# Revit family: Plumbing_Joints_Aignep_Male-Tube-Ball-Valve-90720
name_source: partatom
category: Pipe Accessories
revit_build: Autodesk Revit 2018 (Build: 20170223_1515(x64)
units: mm (PartAtom-declared; Revit-internal decimal feet)

## family parameters
Always vertical = Yes
Cut with Voids When Loaded = No
OmniClass Number = 23.27.43.00
OmniClass Title = Pipe Fittings
Part Type = Valve - Breaks Into
Round Connector Dimension = Use Diameter
Shared = No
Work Plane-Based = No

## types (2) — shared parameters
Assembly Code = D2040100
BIMobject category = Valves
Description = Male-tube ball valve
Design country = Italy
Edition number = 1
IFC Classification = Pipe Fitting
Keynote = 15410
Lookup Table Name = Valve - Male-Tube-Ball-Valve-90720
M = 45 mm
Manufacturer = Aignep Spa
Manufacturer country = Italy
Manufacturer name = Aignep Spa
Material main = Brass
Model = 90720
OmniClass Code = 23-27 43 00
OmniClass Description = Pipe Fittings
Product Guid = 4f6d1d28-9b66-4a88-98e0-9f4e2d31ef23
Product Material = AIGNEP - Brass - Yellow
Product SKU = Male-Tube-Ball-Valve-90720
Product certification = https://www.aignep.com
Product data url = https://www.bimobject.com
Product family = INFINITY
Product group = Valves
Product name = Male-Tube Ball Valve - 90720
Product url = https://www.aignep.com
QR code = https://www.bimobject.com
URL = https://www.aignep.com

## per-type parameters (varying)
| type | A | B | C | CH1 | CH2 | Diameter | E | G | H | H Nut 1 | H Nut 2 | H1 | H2 | H3 | L | M Diameter 1 | M Diameter 2 | Nominal Diameter 01 | Nominal Diameter 02 | Nut Radius 1 | Nut Radius 2 | R | Tick Size 01 | Tick Size 02 |
| D 25 | 16.5 mm | 37 mm | 30.8 mm | 41 mm | 35 mm | 26 mm | 42.5 mm | 106 mm  [stored 0.347769 ft] | 47.5 mm | 11.06 mm | 9.64 mm | 4.069 mm | 1.38 mm | 8.83 mm | 115.1 mm | 43.5 mm | 45 mm | 25.000 mm | 19.050 mm | 21.5 mm | 21.5 mm | 7 mm  [stored 0.0229659 ft] | 20 mm  [stored 0.0656168 ft] | 15.24 mm |
| D 20 | 14 mm  [stored 0.0459318 ft] | 31.5 mm  [stored 0.103346 ft] | 29.3 mm  [stored 0.0961286 ft] | 32 mm  [stored 0.104987 ft] | 30 mm | 20.9 mm | 34.5 mm  [stored 0.113189 ft] | 88 mm  [stored 0.288714 ft] | 42 mm  [stored 0.137795 ft] | 13.084 mm | 6.578 mm | 2.34 mm  [stored 0.00767716 ft] | 0.9 mm  [stored 0.00295276 ft] | 7.817 mm  [stored 0.0256463 ft] | 99.35 mm  [stored 0.325951 ft] | 35.57 mm | 37 mm | 20.000 mm | 12.700 mm | 17 mm  [stored 0.0557743 ft] | 17 mm  [stored 0.0557743 ft] | 5 mm  [stored 0.0164042 ft] | 16 mm  [stored 0.0524934 ft] | 10.16 mm  [stored 0.0333333 ft] |

note: [stored X ft] marks values corroborated as IEEE doubles in the binary element streams (Revit-internal decimal feet)

## geometry (parser evidence)
native form markers: Sweep x6
no freeform markers — native parametric forms only
